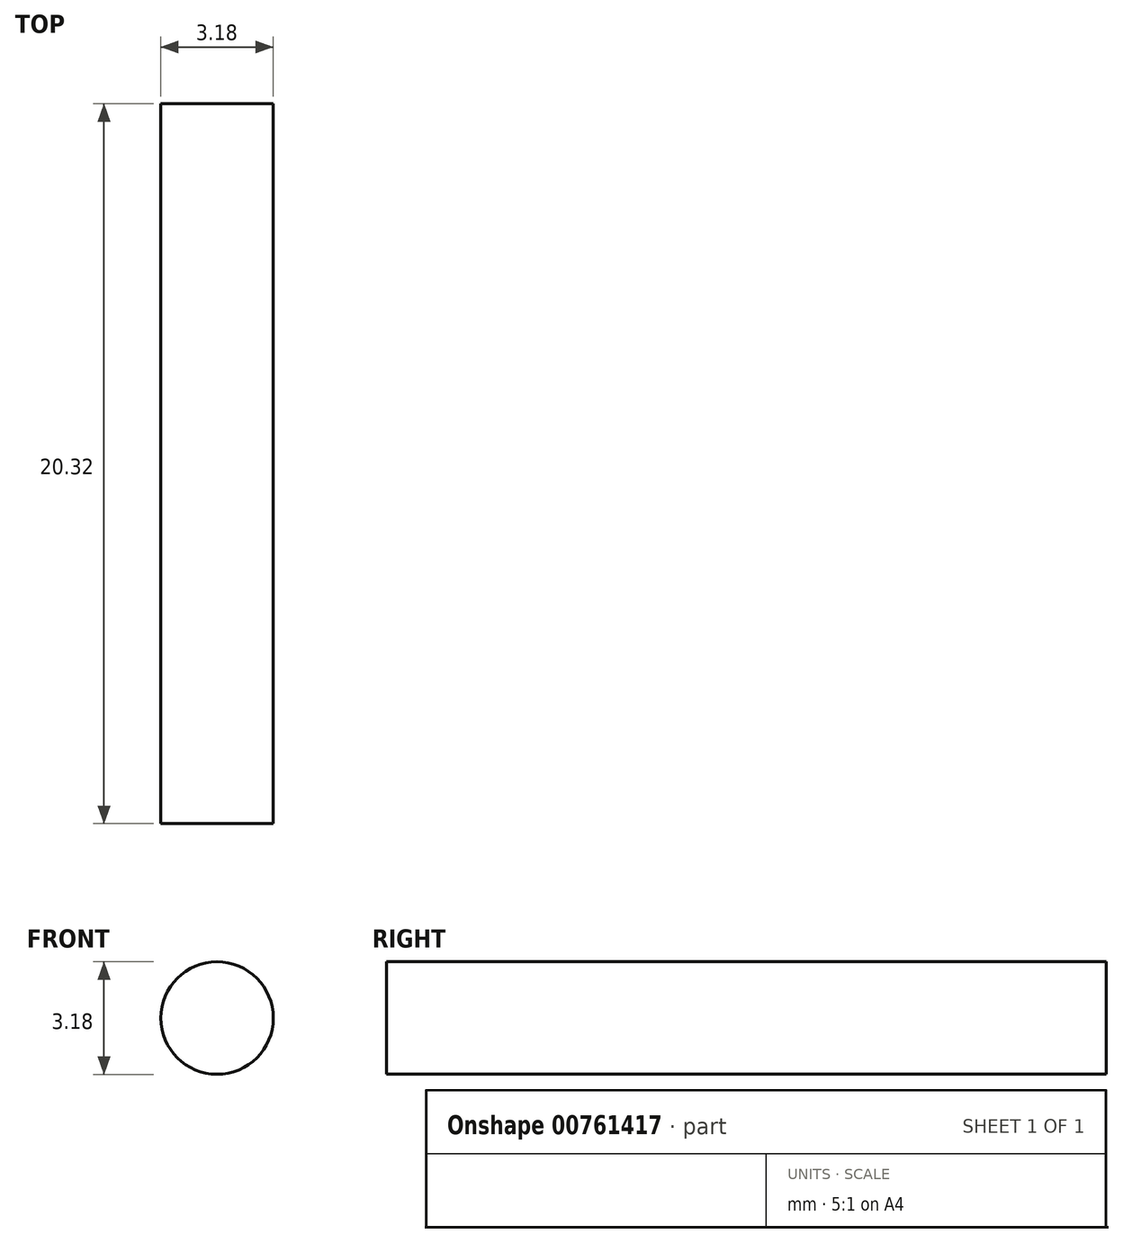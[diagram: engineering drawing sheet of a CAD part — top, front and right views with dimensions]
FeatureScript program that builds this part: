
annotation { "Feature Type Name" : "Feature", "Feature Type Description" : "" }
export const myFeature = defineFeature(function(context is Context, id is Id, definition is map)
    precondition{}
    {
        {
            var Q0;
            Q0=qCreatedBy(makeId("Front.planeOp"),FACE);
            var sketch = newSketch(context, id + "F0", { "sketchPlane" : qUnion([Q0])});
            skCircle(sketch, "E0", {"center": v(0, 0) * mm, "radius": 1.59 * mm});
            skSolve(sketch);
        }
        {
            var Q0;
            Q0=makeQuery(id+"F0.imprint","IMPRINT",FACE,{"disambiguationData":[TD([[makeQuery(id+"F0.imprint","IMPRINT",EDGE,{"derivedFrom":sQuery(id+"F0.wireOp",EDGE,"E0")}),1.0]])]});
            extrude(context, id + "F1", {"entities" : qUnion([Q0]), "depth" : 20.32 * mm, "offsetDistance" : 25.4 * mm});
        }
    });
